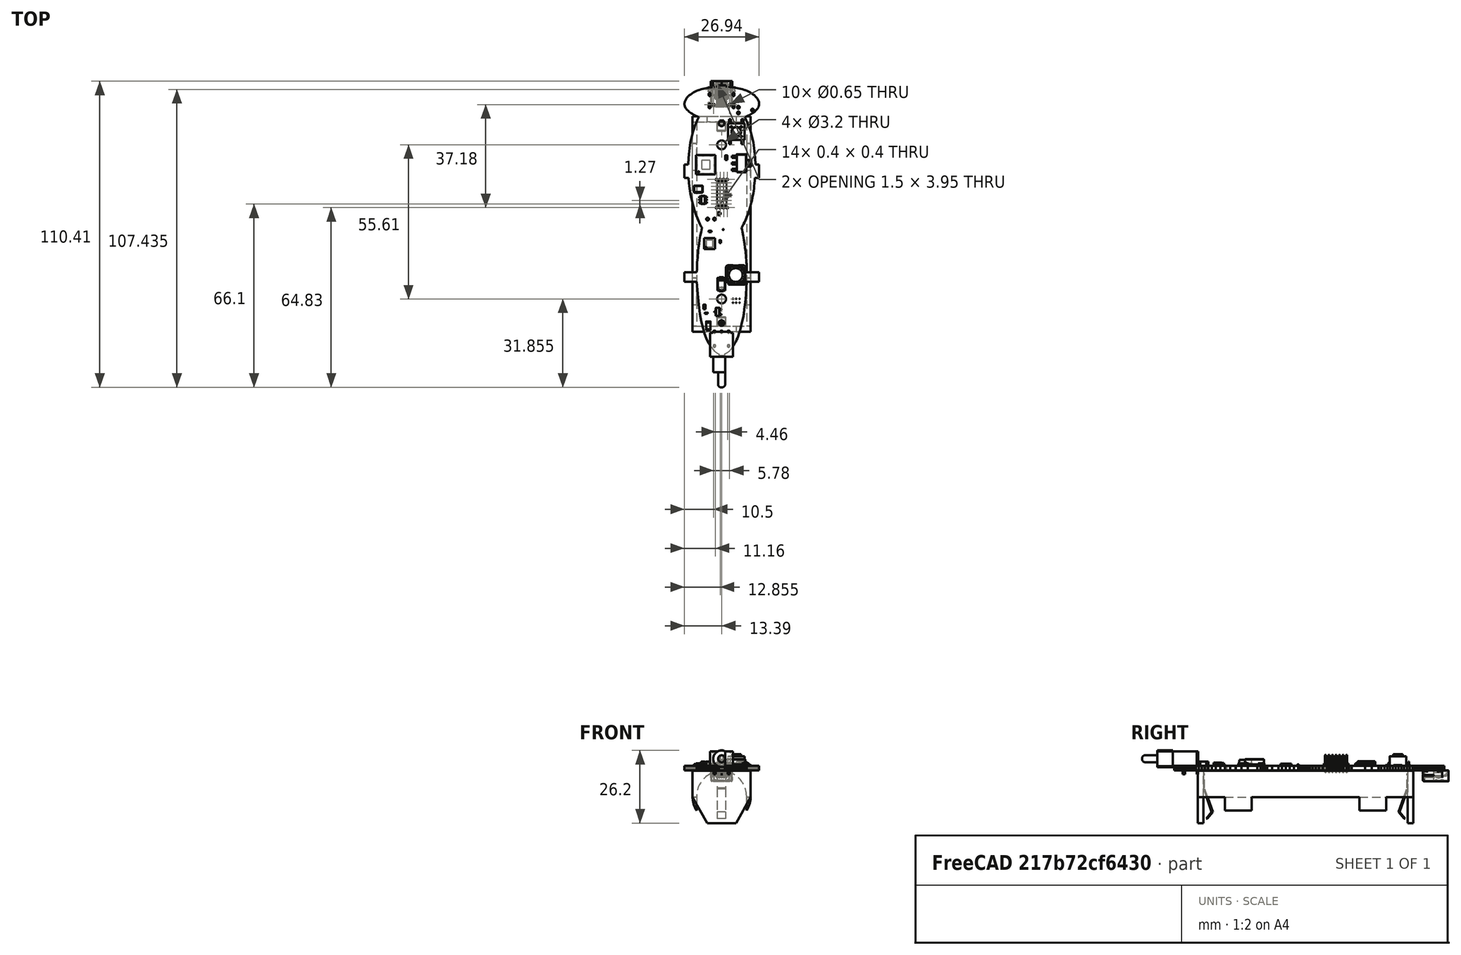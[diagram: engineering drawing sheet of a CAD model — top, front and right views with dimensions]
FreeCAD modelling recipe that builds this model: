
FCSTD DOCUMENT  (FreeCAD 0.21R30454 (Git))
Label: centerBoard
License: All rights reserved
LicenseURL: http://en.wikipedia.org/wiki/All_rights_reserved
objects: App::Link×64, Part::Feature×20, App::Part×5, PartDesign::CoordinateSystem×1, Sketcher::SketchObject×1
note: 22 computed .brp shape members not serialized (recipe doc carries the construction recipe); baked Part::Feature solids carry a one-line shape summary decoded from their .brp

FEATURE [PartDesign::CoordinateSystem] Local_CS_931
  AttacherType = Attacher::AttachEngine3D
  MapMode = 2
  Support = -> [X_Axis001]
FEATURE [Part::Feature] Pcb_931
  shape: bbox 26.94 x 97.45 x 1.6 mm, 316 faces (baked)
FEATURE [Sketcher::SketchObject] PCB_Sketch_931
  FullyConstrained = false
  sketch-geometry (258):
    g0: LineSegment StartX=204.611 StartY=-59.7706 StartZ=0 EndX=204.161 EndY=-58.747 EndZ=0
    g1: LineSegment StartX=207.307 StartY=-79.6422 StartZ=0 EndX=208.849 EndY=-79.6422 EndZ=0
    g2: LineSegment StartX=203.133 StartY=-100.504 StartZ=0 EndX=202.842 EndY=-99.0355 EndZ=0
    g3: LineSegment StartX=198.204 StartY=-141.964 StartZ=0 EndX=198.335 EndY=-141.829 EndZ=0
    g4: LineSegment StartX=196.821 StartY=-46.2543 StartZ=0 EndX=195.381 EndY=-46.2543 EndZ=0
    g5: LineSegment StartX=186.994 StartY=-104.828 StartZ=0 EndX=186.849 EndY=-106.147 EndZ=0
    g6: LineSegment StartX=190.699 StartY=-139.374 StartZ=0 EndX=191.002 EndY=-139.905 EndZ=0
    g7: LineSegment StartX=194.282 StartY=-143.161 StartZ=0 EndX=194.282 EndY=-143.702 EndZ=0
    g8: LineSegment StartX=206.155 StartY=-49.1673 StartZ=0 EndX=205.642 EndY=-48.8567 EndZ=0
    g9: LineSegment StartX=207.546 StartY=-55.4632 StartZ=0 EndX=207.833 EndY=-55.1801 EndZ=0
    g10: LineSegment StartX=191.879 StartY=-141.193 StartZ=0 EndX=192.157 EndY=-141.532 EndZ=0
    g11: LineSegment StartX=186.361 StartY=-117.075 StartZ=0 EndX=186.651 EndY=-121.509 EndZ=0
    g12: LineSegment StartX=208.789 StartY=-53.5041 StartZ=0 EndX=208.834 EndY=-53.2317 EndZ=0
    g13: LineSegment StartX=206.019 StartY=-88.581 StartZ=0 EndX=206.204 EndY=-87.8001 EndZ=0
    g14: LineSegment StartX=203.931 StartY=-123.5 StartZ=0 EndX=204.11 EndY=-121.509 EndZ=0
    g15: LineSegment StartX=183.585 StartY=-81.6183 StartZ=0 EndX=183.791 EndY=-83.5056 EndZ=0
    g16: LineSegment StartX=201.902 StartY=-134.849 StartZ=0 EndX=202.197 EndY=-133.815 EndZ=0
    g17: LineSegment StartX=202.746 StartY=-97.2753 StartZ=0 EndX=202.978 EndY=-96.8717 EndZ=0
    g18: LineSegment StartX=202.76 StartY=-131.45 StartZ=0 EndX=203.025 EndY=-130.106 EndZ=0
    g19: LineSegment StartX=184.261 StartY=-65.7953 StartZ=0 EndX=184.058 EndY=-66.826 EndZ=0
    g20: LineSegment StartX=202.505 StartY=-97.6016 StartZ=0 EndX=202.585 EndY=-97.5204 EndZ=0
    g21: LineSegment StartX=196.48 StartY=-143.161 StartZ=0 EndX=196.623 EndY=-143.098 EndZ=0
    g22: LineSegment StartX=185.289 StartY=-56.8742 StartZ=0 EndX=185.841 EndY=-57.153 EndZ=0
    g23: LineSegment StartX=208.834 StartY=-53.2317 StartZ=0 EndX=208.851 EndY=-52.9624 EndZ=0
    g24: LineSegment StartX=204.4 StartY=-117.075 StartZ=0 EndX=208.849 EndY=-117.075 EndZ=0
    g25: LineSegment StartX=185.651 StartY=-48.576 StartZ=0 EndX=185.119 EndY=-48.8567 EndZ=0
    g26: LineSegment StartX=200.369 StartY=-138.788 StartZ=0 EndX=200.678 EndY=-138.143 EndZ=0
    g27: LineSegment StartX=185.964 StartY=-92.6642 StartZ=0 EndX=186.78 EndY=-94.7637 EndZ=0
    g28: LineSegment StartX=198.468 StartY=-141.686 StartZ=0 EndX=198.604 EndY=-141.532 EndZ=0
    g29: LineSegment StartX=200.262 StartY=-47.1518 StartZ=0 EndX=199.594 EndY=-47.0453 EndZ=0
    g30: LineSegment StartX=186.393 StartY=-112.527 StartZ=0 EndX=186.377 EndY=-113.724 EndZ=0
    g31: LineSegment StartX=182.209 StartY=-51.6716 StartZ=0 EndX=182.103 EndY=-51.9211 EndZ=0
    g32: LineSegment StartX=187.169 StartY=-103.429 StartZ=0 EndX=186.994 EndY=-104.828 EndZ=0
    g33: LineSegment StartX=197.156 StartY=-142.81 StartZ=0 EndX=197.366 EndY=-142.672 EndZ=0
    g34: LineSegment StartX=203.992 StartY=-48.0954 StartZ=0 EndX=203.408 EndY=-47.8915 EndZ=0
    g35: LineSegment StartX=200.678 StartY=-138.143 StartZ=0 EndX=200.987 EndY=-137.433 EndZ=0
    g36: LineSegment StartX=191.301 StartY=-140.383 StartZ=0 EndX=191.593 EndY=-140.811 EndZ=0
    g37: LineSegment StartX=186.503 StartY=-110.129 StartZ=0 EndX=186.46 EndY=-110.807 EndZ=0
    g38: LineSegment StartX=183.377 StartY=-72.3896 StartZ=0 EndX=183.215 EndY=-74.8986 EndZ=0
    g39: LineSegment StartX=206.647 StartY=-49.5098 StartZ=0 EndX=206.155 EndY=-49.1673 EndZ=0
    g40: LineSegment StartX=201.601 StartY=-135.792 StartZ=0 EndX=201.902 EndY=-134.849 EndZ=0
    g41: LineSegment StartX=203.408 StartY=-47.8915 StartZ=0 EndX=202.807 EndY=-47.709 EndZ=0
    g42: LineSegment StartX=208.428 StartY=-51.4271 StartZ=0 EndX=208.284 EndY=-51.188 EndZ=0
    g43: LineSegment StartX=182.294 StartY=-54.3351 StartZ=0 EndX=182.469 EndY=-54.6157 EndZ=0
    g44: LineSegment StartX=185.119 StartY=-48.8567 StartZ=0 EndX=184.607 EndY=-49.1673 EndZ=0
    g45: LineSegment StartX=204.382 StartY=-93.7798 StartZ=0 EndX=204.798 EndY=-92.6642 EndZ=0
    g46: LineSegment StartX=183.215 StartY=-74.8986 StartZ=0 EndX=181.912 EndY=-74.8986 EndZ=0
    g47: LineSegment StartX=205.216 StartY=-91.4223 StartZ=0 EndX=205.627 EndY=-90.0595 EndZ=0
    g48: LineSegment StartX=208.849 StartY=-74.8986 StartZ=0 EndX=207.546 EndY=-74.8986 EndZ=0
    g49: LineSegment StartX=186.651 StartY=-121.509 StartZ=0 EndX=187.031 EndY=-125.349 EndZ=0
    g50: LineSegment StartX=204.125 StartY=-108.431 StartZ=0 EndX=203.913 EndY=-106.147 EndZ=0
    g51: LineSegment StartX=187.38 StartY=-101.978 StartZ=0 EndX=187.169 EndY=-103.429 EndZ=0
    g52: LineSegment StartX=183.913 StartY=-56.0295 StartZ=0 EndX=184.326 EndY=-56.3121 EndZ=0
    g53: LineSegment StartX=205.11 StartY=-48.576 StartZ=0 EndX=204.56 EndY=-48.3229 EndZ=0
    g54: LineSegment StartX=201.561 StartY=-47.4 StartZ=0 EndX=200.918 EndY=-47.2693 EndZ=0
    g55: LineSegment StartX=204.258 StartY=-110.129 StartZ=0 EndX=204.2 EndY=-109.347 EndZ=0
    g56: LineSegment StartX=193.978 StartY=-143.02 StartZ=0 EndX=194.282 EndY=-143.161 EndZ=0
    g57: LineSegment StartX=181.958 StartY=-52.4338 StartZ=0 EndX=181.922 EndY=-52.6963 EndZ=0
    g58: LineSegment StartX=204.798 StartY=-92.6642 StartZ=0 EndX=205.216 EndY=-91.4223 EndZ=0
    g59: LineSegment StartX=204.302 StartY=-110.807 StartZ=0 EndX=204.258 EndY=-110.129 EndZ=0
    g60: LineSegment StartX=196.623 StartY=-143.098 StartZ=0 EndX=196.784 EndY=-143.02 EndZ=0
    g61: LineSegment StartX=198.227 StartY=-46.857 StartZ=0 EndX=196.821 EndY=-46.6878 EndZ=0
    g62: LineSegment StartX=204.56 StartY=-48.3229 StartZ=0 EndX=203.992 EndY=-48.0954 EndZ=0
    g63: LineSegment StartX=183.726 StartY=-68.9546 StartZ=0 EndX=183.593 EndY=-70.0623 EndZ=0
    g64: LineSegment StartX=200.215 StartY=-139.088 StartZ=0 EndX=200.369 EndY=-138.788 EndZ=0
    g65: LineSegment StartX=207.117 StartY=-49.8853 StartZ=0 EndX=206.647 EndY=-49.5098 EndZ=0
    g66: LineSegment StartX=181.972 StartY=-53.5041 StartZ=0 EndX=182.047 EndY=-53.779 EndZ=0
    g67: LineSegment StartX=184.607 StartY=-49.1673 StartZ=0 EndX=184.114 EndY=-49.5098 EndZ=0
    g68: LineSegment StartX=199.61 StartY=-140.15 StartZ=0 EndX=199.759 EndY=-139.905 EndZ=0
    g69: LineSegment StartX=205.627 StartY=-90.0595 StartZ=0 EndX=206.019 EndY=-88.581 EndZ=0
    g70: LineSegment StartX=202.679 StartY=-98.3125 StartZ=0 EndX=202.505 EndY=-97.6016 EndZ=0
    g71: LineSegment StartX=196.962 StartY=-142.925 StartZ=0 EndX=197.156 EndY=-142.81 EndZ=0
    g72: LineSegment StartX=206.204 StartY=-87.8001 StartZ=0 EndX=206.381 EndY=-86.9923 EndZ=0
    g73: LineSegment StartX=198.604 StartY=-141.532 StartZ=0 EndX=198.742 EndY=-141.368 EndZ=0
    g74: LineSegment StartX=189.774 StartY=-137.433 StartZ=0 EndX=190.393 EndY=-138.788 EndZ=0
    g75: LineSegment StartX=184.058 StartY=-66.826 StartZ=0 EndX=183.88 EndY=-67.8774 EndZ=0
    g76: LineSegment StartX=189.16 StartY=-135.792 StartZ=0 EndX=189.774 EndY=-137.433 EndZ=0
    g77: LineSegment StartX=186.151 StartY=-59.7706 StartZ=0 EndX=185.743 EndY=-60.7805 EndZ=0
    g78: LineSegment StartX=206.381 StartY=-86.9923 StartZ=0 EndX=206.547 EndY=-86.1583 EndZ=0
    g79: LineSegment StartX=208.84 StartY=-52.6963 StartZ=0 EndX=208.803 EndY=-52.4338 EndZ=0
    g80: LineSegment StartX=204.318 StartY=-57.4299 StartZ=0 EndX=204.92 EndY=-57.153 EndZ=0
    g81: LineSegment StartX=188.015 StartY=-97.2753 StartZ=0 EndX=188.257 EndY=-97.6016 EndZ=0
    g82: LineSegment StartX=205.472 StartY=-56.8742 StartZ=0 EndX=205.977 EndY=-56.5938 EndZ=0
    g83: LineSegment StartX=185.134 StartY=-90.0595 StartZ=0 EndX=185.545 EndY=-91.4223 EndZ=0
    g84: LineSegment StartX=203.512 StartY=-127.062 StartZ=0 EndX=203.731 EndY=-125.349 EndZ=0
    g85: LineSegment StartX=202.807 StartY=-47.709 StartZ=0 EndX=202.191 EndY=-47.5458 EndZ=0
    g86: LineSegment StartX=189.843 StartY=-47.2693 StartZ=0 EndX=189.2 EndY=-47.4 EndZ=0
    g87: LineSegment StartX=203.025 StartY=-130.106 StartZ=0 EndX=203.276 EndY=-128.645 EndZ=0
    g88: LineSegment StartX=199.314 StartY=-140.603 StartZ=0 EndX=199.461 EndY=-140.383 EndZ=0
    g89: LineSegment StartX=207.169 StartY=-70.0623 StartZ=0 EndX=207.035 EndY=-68.9546 EndZ=0
    g90: LineSegment StartX=199.461 StartY=-140.383 StartZ=0 EndX=199.61 EndY=-140.15 EndZ=0
    g91: LineSegment StartX=191.002 StartY=-139.905 StartZ=0 EndX=191.301 EndY=-140.383 EndZ=0
    g92: LineSegment StartX=186.46 StartY=-110.807 StartZ=0 EndX=186.429 EndY=-111.412 EndZ=0
    g93: LineSegment StartX=182.638 StartY=-50.9546 StartZ=0 EndX=182.477 EndY=-51.188 EndZ=0
    g94: LineSegment StartX=196.821 StartY=-46.6878 StartZ=0 EndX=196.821 EndY=-46.2543 EndZ=0
    g95: LineSegment StartX=183.543 StartY=-55.7465 StartZ=0 EndX=183.913 EndY=-56.0295 EndZ=0
    g96: LineSegment StartX=181.912 StartY=-117.075 StartZ=0 EndX=186.361 EndY=-117.075 EndZ=0
    g97: LineSegment StartX=204.2 StartY=-109.347 StartZ=0 EndX=204.125 EndY=-108.431 EndZ=0
    g98: LineSegment StartX=181.911 StartY=-52.9624 StartZ=0 EndX=181.927 EndY=-53.2317 EndZ=0
    g99: LineSegment StartX=206.702 StartY=-85.2987 StartZ=0 EndX=206.844 EndY=-84.4142 EndZ=0
    g100: LineSegment StartX=208.742 StartY=-52.1753 StartZ=0 EndX=208.658 EndY=-51.9211 EndZ=0
    g101: LineSegment StartX=192.686 StartY=-142.089 StartZ=0 EndX=192.935 EndY=-142.314 EndZ=0
    g102: LineSegment StartX=187.095 StartY=-57.7046 StartZ=0 EndX=186.6 EndY=-58.747 EndZ=0
    g103: LineSegment StartX=208.849 StartY=-117.075 StartZ=0 EndX=208.849 EndY=-113.724 EndZ=0
    g104: LineSegment StartX=196.784 StartY=-143.02 StartZ=0 EndX=196.962 EndY=-142.925 EndZ=0
    g105: LineSegment StartX=186.6 StartY=-58.747 StartZ=0 EndX=186.151 EndY=-59.7706 EndZ=0
    g106: LineSegment StartX=184.785 StartY=-56.5938 StartZ=0 EndX=185.289 EndY=-56.8742 EndZ=0
    g107: LineSegment StartX=198.882 StartY=-141.193 StartZ=0 EndX=199.024 EndY=-141.008 EndZ=0
    g108: LineSegment StartX=191.167 StartY=-47.0453 StartZ=0 EndX=189.843 EndY=-47.2693 EndZ=0
    g109: LineSegment StartX=182.103 StartY=-51.9211 StartZ=0 EndX=182.019 EndY=-52.1753 EndZ=0
    g110: LineSegment StartX=200.918 StartY=-47.2693 StartZ=0 EndX=200.262 EndY=-47.1518 EndZ=0
    g111: LineSegment StartX=203.268 StartY=-96.315 StartZ=0 EndX=203.607 EndY=-95.6105 EndZ=0
    g112: LineSegment StartX=188.565 StartY=-133.815 StartZ=0 EndX=189.16 EndY=-135.792 EndZ=0
    g113: LineSegment StartX=207.218 StartY=-55.7465 StartZ=0 EndX=207.546 EndY=-55.4632 EndZ=0
    g114: LineSegment StartX=207.252 StartY=-80.641 StartZ=0 EndX=207.307 EndY=-79.6422 EndZ=0
    g115: LineSegment StartX=188.257 StartY=-97.6016 StartZ=0 EndX=187.92 EndY=-99.0355 EndZ=0
    g116: LineSegment StartX=186.443 StartY=-57.4299 StartZ=0 EndX=187.095 EndY=-57.7046 EndZ=0
    g117: LineSegment StartX=203.607 StartY=-95.6105 StartZ=0 EndX=203.982 EndY=-94.7637 EndZ=0
    g118: LineSegment StartX=207.554 StartY=-50.2921 StartZ=0 EndX=207.117 EndY=-49.8853 EndZ=0
    g119: LineSegment StartX=185.841 StartY=-57.153 StartZ=0 EndX=186.443 EndY=-57.4299 EndZ=0
    g120: LineSegment StartX=204.267 StartY=-119.37 StartZ=0 EndX=204.4 EndY=-117.075 EndZ=0
    g121: LineSegment StartX=199.168 StartY=-140.811 StartZ=0 EndX=199.314 EndY=-140.603 EndZ=0
    g122: LineSegment StartX=199.91 StartY=-139.646 StartZ=0 EndX=200.062 EndY=-139.374 EndZ=0
    g123: LineSegment StartX=203.731 StartY=-125.349 StartZ=0 EndX=203.931 EndY=-123.5 EndZ=0
    g124: LineSegment StartX=206.844 StartY=-84.4142 StartZ=0 EndX=206.971 EndY=-83.5056 EndZ=0
    g125: LineSegment StartX=203.913 StartY=-106.147 StartZ=0 EndX=203.768 EndY=-104.828 EndZ=0
    g126: LineSegment StartX=206.848 StartY=-56.0295 StartZ=0 EndX=207.218 EndY=-55.7465 EndZ=0
    g127: LineSegment StartX=198.335 StartY=-141.829 StartZ=0 EndX=198.468 EndY=-141.686 EndZ=0
    g128: LineSegment StartX=204.333 StartY=-111.412 StartZ=0 EndX=204.302 EndY=-110.807 EndZ=0
    g129: LineSegment StartX=183.004 StartY=-50.5063 StartZ=0 EndX=182.814 EndY=-50.7272 EndZ=0
    g130: LineSegment StartX=183.88 StartY=-67.8774 StartZ=0 EndX=183.726 EndY=-68.9546 EndZ=0
    g131: LineSegment StartX=181.912 StartY=-79.6422 StartZ=0 EndX=183.454 EndY=-79.6422 EndZ=0
    g132: LineSegment StartX=198.075 StartY=-142.089 StartZ=0 EndX=198.204 EndY=-141.964 EndZ=0
    g133: LineSegment StartX=200.062 StartY=-139.374 StartZ=0 EndX=200.215 EndY=-139.088 EndZ=0
    g134: LineSegment StartX=185.545 StartY=-91.4223 StartZ=0 EndX=185.964 EndY=-92.6642 EndZ=0
    g135: LineSegment StartX=202.978 StartY=-96.8717 StartZ=0 EndX=203.268 EndY=-96.315 EndZ=0
    g136: LineSegment StartX=205.018 StartY=-60.7805 StartZ=0 EndX=204.611 EndY=-59.7706 EndZ=0
    g137: LineSegment StartX=187.954 StartY=-47.709 StartZ=0 EndX=187.354 EndY=-47.8915 EndZ=0
    g138: LineSegment StartX=208.292 StartY=-54.6157 StartZ=0 EndX=208.467 EndY=-54.3351 EndZ=0
    g139: LineSegment StartX=187.92 StartY=-99.0355 StartZ=0 EndX=187.629 EndY=-100.504 EndZ=0
    g140: LineSegment StartX=208.658 StartY=-51.9211 StartZ=0 EndX=208.553 EndY=-51.6716 EndZ=0
    g141: LineSegment StartX=188.002 StartY=-131.45 StartZ=0 EndX=188.565 EndY=-133.815 EndZ=0
    g142: LineSegment StartX=204.11 StartY=-121.509 StartZ=0 EndX=204.267 EndY=-119.37 EndZ=0
    g143: LineSegment StartX=196.48 StartY=-143.702 StartZ=0 EndX=196.48 EndY=-143.161 EndZ=0
    g144: LineSegment StartX=183.791 StartY=-83.5056 StartZ=0 EndX=184.059 EndY=-85.2987 EndZ=0
    g145: LineSegment StartX=193.605 StartY=-142.81 StartZ=0 EndX=193.8 EndY=-142.925 EndZ=0
    g146: LineSegment StartX=186.636 StartY=-108.431 StartZ=0 EndX=186.503 EndY=-110.129 EndZ=0
    g147: LineSegment StartX=192.535 StartY=-46.857 StartZ=0 EndX=191.167 EndY=-47.0453 EndZ=0
    g148: LineSegment StartX=198.742 StartY=-141.368 StartZ=0 EndX=198.882 EndY=-141.193 EndZ=0
    g149: LineSegment StartX=182.814 StartY=-50.7272 StartZ=0 EndX=182.638 EndY=-50.9546 EndZ=0
    g150: LineSegment StartX=187.031 StartY=-125.349 StartZ=0 EndX=187.486 EndY=-128.645 EndZ=0
    g151: LineSegment StartX=183.421 StartY=-50.085 StartZ=0 EndX=183.207 EndY=-50.2921 EndZ=0
    g152: LineSegment StartX=204.368 StartY=-112.527 StartZ=0 EndX=204.354 EndY=-111.975 EndZ=0
    g153: LineSegment StartX=202.585 StartY=-97.5204 StartZ=0 EndX=202.746 EndY=-97.2753 EndZ=0
    g154: LineSegment StartX=184.742 StartY=-88.581 StartZ=0 EndX=185.134 EndY=-90.0595 EndZ=0
    g155: LineSegment StartX=183.454 StartY=-79.6422 StartZ=0 EndX=183.585 EndY=-81.6183 EndZ=0
    g156: LineSegment StartX=206.971 StartY=-83.5056 StartZ=0 EndX=207.082 EndY=-82.5734 EndZ=0
    g157: LineSegment StartX=206.704 StartY=-66.826 StartZ=0 EndX=206.501 EndY=-65.7953 EndZ=0
    g158: LineSegment StartX=203.592 StartY=-103.429 StartZ=0 EndX=203.382 EndY=-101.978 EndZ=0
    g159: LineSegment StartX=208.714 StartY=-53.779 StartZ=0 EndX=208.789 EndY=-53.5041 EndZ=0
    g160: LineSegment StartX=203.276 StartY=-128.645 StartZ=0 EndX=203.512 EndY=-127.062 EndZ=0
    g161: LineSegment StartX=186.429 StartY=-111.412 StartZ=0 EndX=186.393 EndY=-112.527 EndZ=0
    g162: LineSegment StartX=197.826 StartY=-142.314 StartZ=0 EndX=198.075 EndY=-142.089 EndZ=0
    g163: LineSegment StartX=193.396 StartY=-142.672 StartZ=0 EndX=193.605 EndY=-142.81 EndZ=0
    g164: LineSegment StartX=208.851 StartY=-52.9624 StartZ=0 EndX=208.84 EndY=-52.6963 EndZ=0
    g165: LineSegment StartX=197.59 StartY=-142.507 StartZ=0 EndX=197.826 EndY=-142.314 EndZ=0
    g166: LineSegment StartX=206.009 StartY=-63.7765 StartZ=0 EndX=205.715 EndY=-62.7784 EndZ=0
    g167: LineSegment StartX=185.743 StartY=-60.7805 StartZ=0 EndX=185.376 EndY=-61.7814 EndZ=0
    g168: LineSegment StartX=195.381 StartY=-143.702 StartZ=0 EndX=196.48 EndY=-143.702 EndZ=0
    g169: LineSegment StartX=183.593 StartY=-70.0623 StartZ=0 EndX=183.377 EndY=-72.3896 EndZ=0
    g170: LineSegment StartX=206.501 StartY=-65.7953 StartZ=0 EndX=206.27 EndY=-64.7804 EndZ=0
    g171: LineSegment StartX=200.987 StartY=-137.433 StartZ=0 EndX=201.296 EndY=-136.651 EndZ=0
    g172: LineSegment StartX=191.593 StartY=-140.811 StartZ=0 EndX=191.879 EndY=-141.193 EndZ=0
    g173: LineSegment StartX=182.154 StartY=-54.0561 StartZ=0 EndX=182.294 EndY=-54.3351 EndZ=0
    g174: LineSegment StartX=208.607 StartY=-54.0561 StartZ=0 EndX=208.714 EndY=-53.779 EndZ=0
    g175: LineSegment StartX=182.047 StartY=-53.779 StartZ=0 EndX=182.154 EndY=-54.0561 EndZ=0
    g176: LineSegment StartX=199.024 StartY=-141.008 StartZ=0 EndX=199.168 EndY=-140.811 EndZ=0
    g177: LineSegment StartX=192.935 StartY=-142.314 StartZ=0 EndX=193.172 EndY=-142.507 EndZ=0
    g178: LineSegment StartX=189.2 StartY=-47.4 StartZ=0 EndX=188.57 EndY=-47.5458 EndZ=0
    g179: LineSegment StartX=182.68 StartY=-54.8975 StartZ=0 EndX=182.928 EndY=-55.1801 EndZ=0
    g180: LineSegment StartX=186.377 StartY=-113.724 StartZ=0 EndX=181.912 EndY=-113.724 EndZ=0
    g181: LineSegment StartX=202.483 StartY=-132.685 StartZ=0 EndX=202.76 EndY=-131.45 EndZ=0
    g182: LineSegment StartX=183.216 StartY=-55.4632 StartZ=0 EndX=183.543 EndY=-55.7465 EndZ=0
    g183: LineSegment StartX=206.435 StartY=-56.3121 StartZ=0 EndX=206.848 EndY=-56.0295 EndZ=0
    g184: LineSegment StartX=184.326 StartY=-56.3121 StartZ=0 EndX=184.785 EndY=-56.5938 EndZ=0
    g185: LineSegment StartX=184.753 StartY=-63.7765 StartZ=0 EndX=184.492 EndY=-64.7804 EndZ=0
    g186: LineSegment StartX=206.27 StartY=-64.7804 StartZ=0 EndX=206.009 EndY=-63.7765 EndZ=0
    g187: LineSegment StartX=186.202 StartY=-48.3229 StartZ=0 EndX=185.651 EndY=-48.576 EndZ=0
    g188: LineSegment StartX=205.385 StartY=-61.7814 StartZ=0 EndX=205.018 EndY=-60.7805 EndZ=0
    g189: LineSegment StartX=208.467 StartY=-54.3351 StartZ=0 EndX=208.607 EndY=-54.0561 EndZ=0
    g190: LineSegment StartX=187.629 StartY=-100.504 StartZ=0 EndX=187.38 EndY=-101.978 EndZ=0
    g191: LineSegment StartX=207.176 StartY=-81.6183 StartZ=0 EndX=207.252 EndY=-80.641 EndZ=0
    g192: LineSegment StartX=208.082 StartY=-54.8975 StartZ=0 EndX=208.292 EndY=-54.6157 EndZ=0
    g193: LineSegment StartX=204.385 StartY=-113.724 StartZ=0 EndX=204.368 EndY=-112.527 EndZ=0
    g194: LineSegment StartX=208.849 StartY=-113.724 StartZ=0 EndX=204.385 EndY=-113.724 EndZ=0
    g195: LineSegment StartX=201.296 StartY=-136.651 StartZ=0 EndX=201.601 EndY=-135.792 EndZ=0
    g196: LineSegment StartX=183.207 StartY=-50.2921 StartZ=0 EndX=183.004 EndY=-50.5063 EndZ=0
    g197: LineSegment StartX=188.57 StartY=-47.5458 StartZ=0 EndX=187.954 EndY=-47.709 EndZ=0
    g198: LineSegment StartX=190.393 StartY=-138.788 StartZ=0 EndX=190.699 EndY=-139.374 EndZ=0
    g199: LineSegment StartX=185.047 StartY=-62.7784 StartZ=0 EndX=184.753 EndY=-63.7765 EndZ=0
    g200: LineSegment StartX=199.594 StartY=-47.0453 StartZ=0 EndX=198.227 EndY=-46.857 EndZ=0
    g201: LineSegment StartX=204.92 StartY=-57.153 StartZ=0 EndX=205.472 EndY=-56.8742 EndZ=0
    g202: LineSegment StartX=207.546 StartY=-74.8986 StartZ=0 EndX=207.384 EndY=-72.3896 EndZ=0
    g203: LineSegment StartX=208.849 StartY=-79.6422 StartZ=0 EndX=208.849 EndY=-74.8986 EndZ=0
    g204: LineSegment StartX=203.382 StartY=-101.978 StartZ=0 EndX=203.133 EndY=-100.504 EndZ=0
    g205: LineSegment StartX=205.977 StartY=-56.5938 StartZ=0 EndX=206.435 EndY=-56.3121 EndZ=0
    g206: LineSegment StartX=185.376 StartY=-61.7814 StartZ=0 EndX=185.047 EndY=-62.7784 EndZ=0
    g207: LineSegment StartX=184.38 StartY=-86.9923 StartZ=0 EndX=184.742 EndY=-88.581 EndZ=0
    g208: LineSegment StartX=193.8 StartY=-142.925 StartZ=0 EndX=193.978 EndY=-143.02 EndZ=0
    g209: LineSegment StartX=181.912 StartY=-74.8986 StartZ=0 EndX=181.912 EndY=-79.6422 EndZ=0
    g210: LineSegment StartX=182.334 StartY=-51.4271 StartZ=0 EndX=182.209 EndY=-51.6716 EndZ=0
    g211: LineSegment StartX=195.381 StartY=-46.2543 StartZ=0 EndX=193.94 EndY=-46.2543 EndZ=0
    g212: LineSegment StartX=181.922 StartY=-52.6963 StartZ=0 EndX=181.911 EndY=-52.9624 EndZ=0
    g213: LineSegment StartX=192.427 StartY=-141.829 StartZ=0 EndX=192.686 EndY=-142.089 EndZ=0
    g214: LineSegment StartX=208.284 StartY=-51.188 StartZ=0 EndX=208.123 EndY=-50.9546 EndZ=0
    g215: LineSegment StartX=186.769 StartY=-48.0954 StartZ=0 EndX=186.202 EndY=-48.3229 EndZ=0
    g216: LineSegment StartX=202.191 StartY=-47.5458 StartZ=0 EndX=201.561 EndY=-47.4 EndZ=0
    g217: LineSegment StartX=183.644 StartY=-49.8853 StartZ=0 EndX=183.421 EndY=-50.085 EndZ=0
    g218: LineSegment StartX=187.354 StartY=-47.8915 StartZ=0 EndX=186.769 EndY=-48.0954 EndZ=0
    g219: LineSegment StartX=197.366 StartY=-142.672 StartZ=0 EndX=197.59 EndY=-142.507 EndZ=0
    g220: LineSegment StartX=207.947 StartY=-50.7272 StartZ=0 EndX=207.554 EndY=-50.2921 EndZ=0
    g221: LineSegment StartX=187.493 StartY=-96.315 StartZ=0 EndX=188.015 EndY=-97.2753 EndZ=0
    g222: LineSegment StartX=192.157 StartY=-141.532 StartZ=0 EndX=192.427 EndY=-141.829 EndZ=0
    g223: LineSegment StartX=184.059 StartY=-85.2987 StartZ=0 EndX=184.38 EndY=-86.9923 EndZ=0
    g224: LineSegment StartX=181.927 StartY=-53.2317 StartZ=0 EndX=181.972 EndY=-53.5041 EndZ=0
    g225: LineSegment StartX=202.197 StartY=-133.815 StartZ=0 EndX=202.483 EndY=-132.685 EndZ=0
    g226: LineSegment StartX=194.282 StartY=-143.702 StartZ=0 EndX=195.381 EndY=-143.702 EndZ=0
    g227: LineSegment StartX=203.982 StartY=-94.7637 StartZ=0 EndX=204.382 EndY=-93.7798 EndZ=0
    g228: LineSegment StartX=184.492 StartY=-64.7804 StartZ=0 EndX=184.261 EndY=-65.7953 EndZ=0
    g229: LineSegment StartX=193.172 StartY=-142.507 StartZ=0 EndX=193.396 EndY=-142.672 EndZ=0
    g230: LineSegment StartX=182.928 StartY=-55.1801 StartZ=0 EndX=183.216 EndY=-55.4632 EndZ=0
    g231: LineSegment StartX=204.161 StartY=-58.747 StartZ=0 EndX=203.666 EndY=-57.7046 EndZ=0
    g232: LineSegment StartX=182.477 StartY=-51.188 StartZ=0 EndX=182.334 EndY=-51.4271 EndZ=0
    g233: LineSegment StartX=199.759 StartY=-139.905 StartZ=0 EndX=199.91 EndY=-139.646 EndZ=0
    g234: LineSegment StartX=187.486 StartY=-128.645 StartZ=0 EndX=188.002 EndY=-131.45 EndZ=0
    g235: LineSegment StartX=205.642 StartY=-48.8567 StartZ=0 EndX=205.11 EndY=-48.576 EndZ=0
    g236: LineSegment StartX=207.035 StartY=-68.9546 StartZ=0 EndX=206.881 EndY=-67.8774 EndZ=0
    g237: LineSegment StartX=181.912 StartY=-113.724 StartZ=0 EndX=181.912 EndY=-117.075 EndZ=0
    g238: LineSegment StartX=208.553 StartY=-51.6716 StartZ=0 EndX=208.428 EndY=-51.4271 EndZ=0
    g239: LineSegment StartX=202.842 StartY=-99.0355 StartZ=0 EndX=202.679 EndY=-98.3125 EndZ=0
    g240: LineSegment StartX=207.384 StartY=-72.3896 StartZ=0 EndX=207.169 EndY=-70.0623 EndZ=0
    g241: LineSegment StartX=186.849 StartY=-106.147 StartZ=0 EndX=186.636 EndY=-108.431 EndZ=0
    g242: LineSegment StartX=208.803 StartY=-52.4338 StartZ=0 EndX=208.742 EndY=-52.1753 EndZ=0
    g243: LineSegment StartX=182.469 StartY=-54.6157 StartZ=0 EndX=182.68 EndY=-54.8975 EndZ=0
    g244: LineSegment StartX=182.019 StartY=-52.1753 StartZ=0 EndX=181.958 EndY=-52.4338 EndZ=0
    g245: LineSegment StartX=203.768 StartY=-104.828 StartZ=0 EndX=203.592 EndY=-103.429 EndZ=0
    g246: LineSegment StartX=206.547 StartY=-86.1583 StartZ=0 EndX=206.702 EndY=-85.2987 EndZ=0
    g247: LineSegment StartX=207.082 StartY=-82.5734 StartZ=0 EndX=207.176 EndY=-81.6183 EndZ=0
    g248: LineSegment StartX=184.114 StartY=-49.5098 StartZ=0 EndX=183.644 EndY=-49.8853 EndZ=0
    g249: LineSegment StartX=207.833 StartY=-55.1801 StartZ=0 EndX=208.082 EndY=-54.8975 EndZ=0
    g250: LineSegment StartX=193.94 StartY=-46.2543 StartZ=0 EndX=193.94 EndY=-46.6878 EndZ=0
    g251: LineSegment StartX=206.881 StartY=-67.8774 StartZ=0 EndX=206.704 EndY=-66.826 EndZ=0
    g252: LineSegment StartX=186.78 StartY=-94.7637 StartZ=0 EndX=187.493 EndY=-96.315 EndZ=0
    g253: LineSegment StartX=204.354 StartY=-111.975 StartZ=0 EndX=204.333 EndY=-111.412 EndZ=0
    g254: LineSegment StartX=203.666 StartY=-57.7046 StartZ=0 EndX=204.318 EndY=-57.4299 EndZ=0
    g255: LineSegment StartX=208.123 StartY=-50.9546 StartZ=0 EndX=207.947 EndY=-50.7272 EndZ=0
    g256: LineSegment StartX=205.715 StartY=-62.7784 StartZ=0 EndX=205.385 EndY=-61.7814 EndZ=0
    g257: LineSegment StartX=193.94 StartY=-46.6878 StartZ=0 EndX=192.535 EndY=-46.857 EndZ=0
  constraints (258):
    c: Coincident(g96,g237)
    c: Coincident(g180,g237)
    c: Coincident(g131,g209)
    c: Coincident(g46,g209)
    c: Coincident(g98,g212)
    c: Coincident(g98,g224)
    c: Coincident(g57,g212)
    c: Coincident(g57,g244)
    c: Coincident(g66,g224)
    c: Coincident(g109,g244)
    c: Coincident(g66,g175)
    c: Coincident(g31,g109)
    c: Coincident(g173,g175)
    c: Coincident(g31,g210)
    c: Coincident(g43,g173)
    c: Coincident(g210,g232)
    c: Coincident(g43,g243)
    c: Coincident(g93,g232)
    c: Coincident(g93,g149)
    c: Coincident(g179,g243)
    c: Coincident(g129,g149)
    c: Coincident(g179,g230)
    c: Coincident(g129,g196)
    c: Coincident(g38,g46)
    c: Coincident(g182,g230)
    c: Coincident(g151,g196)
    c: Coincident(g38,g169)
    c: Coincident(g151,g217)
    c: Coincident(g131,g155)
    c: Coincident(g95,g182)
    c: Coincident(g15,g155)
    c: Coincident(g63,g169)
    c: Coincident(g217,g248)
    c: Coincident(g63,g130)
    c: Coincident(g15,g144)
    c: Coincident(g75,g130)
    c: Coincident(g52,g95)
    c: Coincident(g144,g223)
    c: Coincident(g19,g75)
    c: Coincident(g67,g248)
    c: Coincident(g19,g228)
    c: Coincident(g52,g184)
    c: Coincident(g207,g223)
    c: Coincident(g185,g228)
    c: Coincident(g44,g67)
    c: Coincident(g154,g207)
    c: Coincident(g185,g199)
    c: Coincident(g106,g184)
    c: Coincident(g199,g206)
    c: Coincident(g25,g44)
    c: Coincident(g83,g154)
    c: Coincident(g22,g106)
    c: Coincident(g167,g206)
    c: Coincident(g83,g134)
    c: Coincident(g25,g187)
    c: Coincident(g77,g167)
    c: Coincident(g22,g119)
    c: Coincident(g27,g134)
    c: Coincident(g77,g105)
    c: Coincident(g187,g215)
    c: Coincident(g11,g96)
    c: Coincident(g30,g180)
    c: Coincident(g30,g161)
    c: Coincident(g92,g161)
    c: Coincident(g116,g119)
    c: Coincident(g37,g92)
    c: Coincident(g37,g146)
    c: Coincident(g102,g105)
    c: Coincident(g146,g241)
    c: Coincident(g11,g49)
    c: Coincident(g215,g218)
    c: Coincident(g27,g252)
    c: Coincident(g5,g241)
    c: Coincident(g5,g32)
    c: Coincident(g49,g150)
    c: Coincident(g102,g116)
    c: Coincident(g32,g51)
    c: Coincident(g137,g218)
    c: Coincident(g51,g190)
    c: Coincident(g150,g234)
    c: Coincident(g221,g252)
    c: Coincident(g139,g190)
    c: Coincident(g115,g139)
    c: Coincident(g137,g197)
    c: Coincident(g141,g234)
    c: Coincident(g81,g221)
    c: Coincident(g81,g115)
    c: Coincident(g112,g141)
    c: Coincident(g178,g197)
    c: Coincident(g76,g112)
    c: Coincident(g86,g178)
    c: Coincident(g74,g76)
    c: Coincident(g86,g108)
    c: Coincident(g74,g198)
    c: Coincident(g6,g198)
    c: Coincident(g6,g91)
    c: Coincident(g108,g147)
    c: Coincident(g36,g91)
    c: Coincident(g36,g172)
    c: Coincident(g10,g172)
    c: Coincident(g10,g222)
    c: Coincident(g213,g222)
    c: Coincident(g147,g257)
    c: Coincident(g101,g213)
    c: Coincident(g101,g177)
    c: Coincident(g177,g229)
    c: Coincident(g163,g229)
    c: Coincident(g145,g163)
    c: Coincident(g145,g208)
    c: Coincident(g250,g257)
    c: Coincident(g211,g250)
    c: Coincident(g56,g208)
    c: Coincident(g7,g226)
    c: Coincident(g7,g56)
    c: Coincident(g168,g226)
    c: Coincident(g4,g211)
    c: Coincident(g143,g168)
    c: Coincident(g21,g143)
    c: Coincident(g21,g60)
    c: Coincident(g60,g104)
    c: Coincident(g61,g94)
    c: Coincident(g4,g94)
    c: Coincident(g71,g104)
    c: Coincident(g33,g71)
    c: Coincident(g33,g219)
    c: Coincident(g165,g219)
    c: Coincident(g162,g165)
    c: Coincident(g132,g162)
    c: Coincident(g3,g132)
    c: Coincident(g61,g200)
    c: Coincident(g3,g127)
    c: Coincident(g28,g127)
    c: Coincident(g28,g73)
    c: Coincident(g73,g148)
    c: Coincident(g107,g148)
    c: Coincident(g107,g176)
    c: Coincident(g121,g176)
    c: Coincident(g88,g121)
    c: Coincident(g88,g90)
    c: Coincident(g29,g200)
    c: Coincident(g68,g90)
    c: Coincident(g68,g233)
    c: Coincident(g122,g233)
    c: Coincident(g122,g133)
    c: Coincident(g64,g133)
    c: Coincident(g29,g110)
    c: Coincident(g26,g64)
    c: Coincident(g26,g35)
    c: Coincident(g54,g110)
    c: Coincident(g35,g171)
    c: Coincident(g171,g195)
    c: Coincident(g54,g216)
    c: Coincident(g40,g195)
    c: Coincident(g16,g40)
    c: Coincident(g16,g225)
    c: Coincident(g85,g216)
    c: Coincident(g181,g225)
    c: Coincident(g20,g70)
    c: Coincident(g20,g153)
    c: Coincident(g70,g239)
    c: Coincident(g17,g153)
    c: Coincident(g18,g181)
    c: Coincident(g41,g85)
    c: Coincident(g2,g239)
    c: Coincident(g17,g135)
    c: Coincident(g18,g87)
    c: Coincident(g2,g204)
    c: Coincident(g87,g160)
    c: Coincident(g111,g135)
    c: Coincident(g158,g204)
    c: Coincident(g34,g41)
    c: Coincident(g84,g160)
    c: Coincident(g158,g245)
    c: Coincident(g111,g117)
    c: Coincident(g231,g254)
    c: Coincident(g84,g123)
    c: Coincident(g125,g245)
    c: Coincident(g50,g125)
    c: Coincident(g14,g123)
    c: Coincident(g117,g227)
    c: Coincident(g34,g62)
    c: Coincident(g14,g142)
    c: Coincident(g50,g97)
    c: Coincident(g0,g231)
    c: Coincident(g55,g97)
    c: Coincident(g120,g142)
    c: Coincident(g55,g59)
    c: Coincident(g59,g128)
    c: Coincident(g80,g254)
    c: Coincident(g128,g253)
    c: Coincident(g152,g253)
    c: Coincident(g152,g193)
    c: Coincident(g193,g194)
    c: Coincident(g45,g227)
    c: Coincident(g24,g120)
    c: Coincident(g53,g62)
    c: Coincident(g0,g136)
    c: Coincident(g45,g58)
    c: Coincident(g80,g201)
    c: Coincident(g136,g188)
    c: Coincident(g53,g235)
    c: Coincident(g47,g58)
    c: Coincident(g188,g256)
    c: Coincident(g82,g201)
    c: Coincident(g47,g69)
    c: Coincident(g8,g235)
    c: Coincident(g166,g256)
    c: Coincident(g82,g205)
    c: Coincident(g166,g186)
    c: Coincident(g13,g69)
    c: Coincident(g8,g39)
    c: Coincident(g13,g72)
    c: Coincident(g170,g186)
    c: Coincident(g72,g78)
    c: Coincident(g183,g205)
    c: Coincident(g157,g170)
    c: Coincident(g78,g246)
    c: Coincident(g39,g65)
    c: Coincident(g99,g246)
    c: Coincident(g157,g251)
    c: Coincident(g99,g124)
    c: Coincident(g126,g183)
    c: Coincident(g236,g251)
    c: Coincident(g124,g156)
    c: Coincident(g89,g236)
    c: Coincident(g156,g247)
    c: Coincident(g65,g118)
    c: Coincident(g191,g247)
    c: Coincident(g89,g240)
    c: Coincident(g113,g126)
    c: Coincident(g114,g191)
    c: Coincident(g1,g114)
    c: Coincident(g202,g240)
    c: Coincident(g48,g202)
    c: Coincident(g9,g113)
    c: Coincident(g118,g220)
    c: Coincident(g9,g249)
    c: Coincident(g220,g255)
    c: Coincident(g192,g249)
    c: Coincident(g214,g255)
    c: Coincident(g138,g192)
    c: Coincident(g42,g214)
    c: Coincident(g42,g238)
    c: Coincident(g138,g189)
    c: Coincident(g140,g238)
    c: Coincident(g174,g189)
    c: Coincident(g100,g140)
    c: Coincident(g159,g174)
    c: Coincident(g100,g242)
    c: Coincident(g12,g159)
    c: Coincident(g79,g242)
    c: Coincident(g12,g23)
    c: Coincident(g24,g103)
    c: Coincident(g103,g194)
    c: Coincident(g1,g203)
    c: Coincident(g48,g203)
    c: Coincident(g79,g164)
    c: Coincident(g23,g164)
FEATURE [App::Part] Board_Geoms_931
  Group = -> [Pcb_931,PCB_Sketch_931]
  Origin = -> Origin
FEATURE [Part::Feature] Shape  label="R21_C_0402_1005Metric_38c94f1f1ba7"
  Placement = pos=(189.8,-128.5,0) rot=(0,0,1;3.14159rad)
  shape: bbox 1 x 0.5 x 0.5 mm, 28 faces (baked)
FEATURE [App::Link] R21_C_0402_1005Metric_38c94f1f1ba7_ln_  label="R20_C_0402_1005Metric_7b8d80ad2dcc"
  LinkPlacement = pos=(189.9,-114.1,0) rot=(0,0,1;3.14159rad)
  LinkedObject = -> Shape
  Placement = pos=(189.9,-114.1,0) rot=(0,0,1;3.14159rad)
FEATURE [App::Link] R21_C_0402_1005Metric_38c94f1f1ba7_ln_001  label="C1_C_0402_1005Metric_d29c508b4b60"
  LinkPlacement = pos=(195.2,-70.7,0) rot=(0,0,1;0rad)
  LinkedObject = -> Shape
  Placement = pos=(195.2,-70.7,0) rot=(0,0,1;0rad)
FEATURE [Part::Feature] Shape001  label="R19_R_0402_1005Metric_9ca80ee487fc"
  Placement = pos=(194.8,-102.6,0) rot=(0,0,-1;1.5708rad)
  shape: bbox 0.5 x 1 x 0.35 mm, 26 faces (baked)
FEATURE [App::Link] R21_C_0402_1005Metric_38c94f1f1ba7_ln_002  label="C9_C_0402_1005Metric_a875c5e367f2"
  LinkPlacement = pos=(190.3,-80.1,0) rot=(0,0,-1;1.5708rad)
  LinkedObject = -> Shape
  Placement = pos=(190.3,-80.1,0) rot=(0,0,-1;1.5708rad)
FEATURE [Part::Feature] Shape002  label="D2_D_SMA_34cf3897dfc1"
  Placement = pos=(195.2,-118,0) rot=(0,0,-1;1.5708rad)
  shape: bbox 2.7 x 5 x 2.22 mm, 41 faces (baked)
FEATURE [Part::Feature] Shape003  label="C42_C_0603_1608Metric_3f0e18eb3bdb"
  Placement = pos=(197,-72.4,0) rot=(0,0,1;1.5708rad)
  shape: bbox 0.8 x 1.6 x 0.8 mm, 28 faces (baked)
FEATURE [Part::Feature] Shape004  label="SW3_Fillet_54ad2342c7e7"
  Placement = pos=(195.3,-140.21,0) rot=(0,0,1;3.14159rad)
  shape: bbox 8.3 x 20.48 x 8.6 mm, 32 faces (baked)
FEATURE [Part::Feature] Shape005  label="U5_SOT_223_0bc22c24d438"
  Placement = pos=(202.5,-74.4,0) rot=(0,0,1;0rad)
  shape: bbox 7 x 6.5 x 1.7 mm, 78 faces (baked)
FEATURE [App::Link] R19_R_0402_1005Metric_9ca80ee487fc_ln_  label="R2_R_0402_1005Metric_dea8e135976e"
  LinkPlacement = pos=(201.5,-68.7,0) rot=(0,0,1;1.5708rad)
  LinkedObject = -> Shape001
  Placement = pos=(201.5,-68.7,0) rot=(0,0,1;1.5708rad)
FEATURE [App::Link] C42_C_0603_1608Metric_3f0e18eb3bdb_ln_  label="C45_C_0603_1608Metric_d322fa890f2c"
  LinkPlacement = pos=(188.9,-123.4,0) rot=(0,0,1;0rad)
  LinkedObject = -> Shape003
  Placement = pos=(188.9,-123.4,0) rot=(0,0,1;0rad)
FEATURE [App::Link] R21_C_0402_1005Metric_38c94f1f1ba7_ln_003  label="C46_C_0402_1005Metric_a9bfb0d6892e"
  LinkPlacement = pos=(189.1,-100.1,0) rot=(0,0,1;0rad)
  LinkedObject = -> Shape
  Placement = pos=(189.1,-100.1,0) rot=(0,0,1;0rad)
FEATURE [App::Link] R19_R_0402_1005Metric_9ca80ee487fc_ln_001  label="R15_R_0402_1005Metric_e6cf502f8789"
  LinkPlacement = pos=(187.7,-106.9,0) rot=(0,0,-1;1.5708rad)
  LinkedObject = -> Shape001
  Placement = pos=(187.7,-106.9,0) rot=(0,0,-1;1.5708rad)
FEATURE [Part::Feature] Shape006  label="C44_C_1206_3216Metric_504a53cc2dd0"
  Placement = pos=(190.5,-133.025,0) rot=(0,0,-1;1.5708rad)
  shape: bbox 1.6 x 3.2 x 1.6 mm, 28 faces (baked)
FEATURE [App::Link] R21_C_0402_1005Metric_38c94f1f1ba7_ln_004  label="C18_C_0402_1005Metric_92a1be41be9e"
  LinkPlacement = pos=(189.4,-106.5,0) rot=(0,0,1;0rad)
  LinkedObject = -> Shape
  Placement = pos=(189.4,-106.5,0) rot=(0,0,1;0rad)
FEATURE [App::Link] R21_C_0402_1005Metric_38c94f1f1ba7_ln_005  label="C31_C_0402_1005Metric_578c4d3870ae"
  LinkPlacement = pos=(189,-90,0) rot=(0,0,1;3.14159rad)
  LinkedObject = -> Shape
  Placement = pos=(189,-90,0) rot=(0,0,1;3.14159rad)
FEATURE [App::Link] R19_R_0402_1005Metric_9ca80ee487fc_ln_002  label="R3_R_0402_1005Metric_969b0b0747f2"
  LinkPlacement = pos=(191.3,-80.09,0) rot=(0,0,-1;1.5708rad)
  LinkedObject = -> Shape001
  Placement = pos=(191.3,-80.09,0) rot=(0,0,-1;1.5708rad)
FEATURE [App::Link] R21_C_0402_1005Metric_38c94f1f1ba7_ln_006  label="C29_C_0402_1005Metric_878fa2face33"
  LinkPlacement = pos=(185.6,-86.9,0) rot=(0,0,1;1.5708rad)
  LinkedObject = -> Shape
  Placement = pos=(185.6,-86.9,0) rot=(0,0,1;1.5708rad)
FEATURE [Part::Feature] Shape007  label="U6_QFN-20-1EP_4x4mm_Pitch0.5mm_3f7a39cb167c"
  Placement = pos=(190.975,-103.35,0) rot=(0,0,1;1.5708rad)
  shape: bbox 4 x 4 x 0.77 mm, 134 faces (baked)
FEATURE [App::Link] R19_R_0402_1005Metric_9ca80ee487fc_ln_003  label="R18_R_0402_1005Metric_e9874ca0240e"
  LinkPlacement = pos=(195.4,-53,0) rot=(0,0,1;1.5708rad)
  LinkedObject = -> Shape001
  Placement = pos=(195.4,-53,0) rot=(0,0,1;1.5708rad)
FEATURE [App::Link] R19_R_0402_1005Metric_9ca80ee487fc_ln_004  label="R7_R_0402_1005Metric_0d6ee2aba382"
  LinkPlacement = pos=(196.1,-57,0) rot=(0,0,-1;1.5708rad)
  LinkedObject = -> Shape001
  Placement = pos=(196.1,-57,0) rot=(0,0,-1;1.5708rad)
FEATURE [Part::Feature] Shape008  label="L3_L_0402_1005Metric_7322f57e24a3"
  Placement = pos=(191.1,-99,0) rot=(0,0,1;3.14159rad)
  shape: bbox 1 x 0.5 x 0.5 mm, 28 faces (baked)
FEATURE [App::Link] C42_C_0603_1608Metric_3f0e18eb3bdb_ln_001  label="C26_C_0603_1608Metric_e24a75b1fd6c"
  LinkPlacement = pos=(196.7,-53.6,0) rot=(0,0,-1;1.5708rad)
  LinkedObject = -> Shape003
  Placement = pos=(196.7,-53.6,0) rot=(0,0,-1;1.5708rad)
FEATURE [App::Link] R21_C_0402_1005Metric_38c94f1f1ba7_ln_007  label="C41_C_0402_1005Metric_e05767d0328b"
  LinkPlacement = pos=(196.7,-101.5,0) rot=(0,0,1;1.5708rad)
  LinkedObject = -> Shape
  Placement = pos=(196.7,-101.5,0) rot=(0,0,1;1.5708rad)
FEATURE [App::Link] R19_R_0402_1005Metric_9ca80ee487fc_ln_005  label="R6_R_0402_1005Metric_11a2181a152e"
  LinkPlacement = pos=(195.1,-57,0) rot=(0,0,-1;1.5708rad)
  LinkedObject = -> Shape001
  Placement = pos=(195.1,-57,0) rot=(0,0,-1;1.5708rad)
FEATURE [App::Link] C44_C_1206_3216Metric_504a53cc2dd0_ln_  label="C15_C_1206_3216Metric_4eda32e8580f"
  LinkPlacement = pos=(204.5,-79.3,0) rot=(0,0,1;0rad)
  LinkedObject = -> Shape006
  Placement = pos=(204.5,-79.3,0) rot=(0,0,1;0rad)
FEATURE [App::Link] C44_C_1206_3216Metric_504a53cc2dd0_ln_001  label="C22_C_1206_3216Metric_2920babed859"
  LinkPlacement = pos=(204.4,-81.8,0) rot=(0,0,1;0rad)
  LinkedObject = -> Shape006
  Placement = pos=(204.4,-81.8,0) rot=(0,0,1;0rad)
FEATURE [App::Link] R19_R_0402_1005Metric_9ca80ee487fc_ln_006  label="R23_R_0402_1005Metric_7dfb490c449e"
  LinkPlacement = pos=(184.1,-52.41,0) rot=(0,0,1;1.5708rad)
  LinkedObject = -> Shape001
  Placement = pos=(184.1,-52.41,0) rot=(0,0,1;1.5708rad)
FEATURE [Part::Feature] Shape009  label="D516_LED_0603_1608Metric_23db4c450fc7"
  Placement = pos=(189.1,-126.2,0) rot=(0,0,1;1.5708rad)
  shape: bbox 0.8 x 1.6 x 1.1 mm, 50 faces (baked)
FEATURE [App::Link] R21_C_0402_1005Metric_38c94f1f1ba7_ln_008  label="C16_C_0402_1005Metric_ccc6f5fbae95"
  LinkPlacement = pos=(192.7,-132.7,0) rot=(0,0,1;1.5708rad)
  LinkedObject = -> Shape
  Placement = pos=(192.7,-132.7,0) rot=(0,0,1;1.5708rad)
FEATURE [App::Link] R21_C_0402_1005Metric_38c94f1f1ba7_ln_009  label="C20_C_0402_1005Metric_339430b002f9"
  LinkPlacement = pos=(204.7,-53.1,0) rot=(0,0,1;3.14159rad)
  LinkedObject = -> Shape
  Placement = pos=(204.7,-53.1,0) rot=(0,0,1;3.14159rad)
FEATURE [App::Link] R21_C_0402_1005Metric_38c94f1f1ba7_ln_010  label="C47_C_0402_1005Metric_af42fe187c16"
  LinkPlacement = pos=(195,-99.9,0) rot=(0,0,1;0rad)
  LinkedObject = -> Shape
  Placement = pos=(195,-99.9,0) rot=(0,0,1;0rad)
FEATURE [Part::Feature] Shape010  label="U8_SOT_23_1e3b1a0e5d43"
  Placement = pos=(193.9,-128,0) rot=(0,0,1;3.14159rad)
  shape: bbox 2.5 x 3 x 1.2 mm, 76 faces (baked)
FEATURE [App::Link] R21_C_0402_1005Metric_38c94f1f1ba7_ln_011  label="C6_C_0402_1005Metric_7f7ff18c55e3"
  LinkPlacement = pos=(190.5,-68.8,0) rot=(0,0,1;3.14159rad)
  LinkedObject = -> Shape
  Placement = pos=(190.5,-68.8,0) rot=(0,0,1;3.14159rad)
FEATURE [App::Link] D2_D_SMA_34cf3897dfc1_ln_  label="D1_D_SMA_3cb871b8a290"
  LinkPlacement = pos=(190.3,-109.8,0) rot=(0,0,1;3.14159rad)
  LinkedObject = -> Shape002
  Placement = pos=(190.3,-109.8,0) rot=(0,0,1;3.14159rad)
FEATURE [Part::Feature] Shape011  label="U3_QFN_56_1EP_7x7mm_P04mm_EP32x32mm_92a982e71d8d"
  Placement = pos=(189.6,-74.9,0) rot=(0,0,1;0rad)
  shape: bbox 7 x 7 x 0.95 mm, 350 faces (baked)
FEATURE [App::Link] R21_C_0402_1005Metric_38c94f1f1ba7_ln_012  label="C30_C_0402_1005Metric_cc59a400e17a"
  LinkPlacement = pos=(191,-90,0) rot=(0,0,1;3.14159rad)
  LinkedObject = -> Shape
  Placement = pos=(191,-90,0) rot=(0,0,1;3.14159rad)
FEATURE [App::Link] R21_C_0402_1005Metric_38c94f1f1ba7_ln_013  label="C13_C_0402_1005Metric_d2173120320b"
  LinkPlacement = pos=(198.8,-57.6,0) rot=(0,0,1;3.14159rad)
  LinkedObject = -> Shape
  Placement = pos=(198.8,-57.6,0) rot=(0,0,1;3.14159rad)
FEATURE [App::Link] L3_L_0402_1005Metric_7322f57e24a3_ln_  label="L4_L_0402_1005Metric_e4c50960bfc8"
  LinkPlacement = pos=(190.7,-97.6,0) rot=(0,0,1;0rad)
  LinkedObject = -> Shape008
  Placement = pos=(190.7,-97.6,0) rot=(0,0,1;0rad)
FEATURE [App::Link] R21_C_0402_1005Metric_38c94f1f1ba7_ln_014  label="C2_C_0402_1005Metric_4b4f118f5010"
  LinkPlacement = pos=(185.6,-81.3,0) rot=(0,0,1;3.14159rad)
  LinkedObject = -> Shape
  Placement = pos=(185.6,-81.3,0) rot=(0,0,1;3.14159rad)
FEATURE [App::Link] D516_LED_0603_1608Metric_23db4c450fc7_ln_  label="D517_LED_0603_1608Metric_b24ae36cc63a"
  LinkPlacement = pos=(190.7,-126.2,0) rot=(0,0,1;1.5708rad)
  LinkedObject = -> Shape009
  Placement = pos=(190.7,-126.2,0) rot=(0,0,1;1.5708rad)
FEATURE [App::Link] R21_C_0402_1005Metric_38c94f1f1ba7_ln_015  label="C10_C_0402_1005Metric_25fd1e42a1bf"
  LinkPlacement = pos=(186.1,-69.6,0) rot=(0,0,1;1.5708rad)
  LinkedObject = -> Shape
  Placement = pos=(186.1,-69.6,0) rot=(0,0,1;1.5708rad)
FEATURE [App::Link] R21_C_0402_1005Metric_38c94f1f1ba7_ln_016  label="C33_C_0402_1005Metric_872bb8822931"
  LinkPlacement = pos=(204.2,-51.5,0) rot=(0,0,-1;1.5708rad)
  LinkedObject = -> Shape
  Placement = pos=(204.2,-51.5,0) rot=(0,0,-1;1.5708rad)
FEATURE [App::Link] R21_C_0402_1005Metric_38c94f1f1ba7_ln_017  label="C43_C_0402_1005Metric_b465c88a99c7"
  LinkPlacement = pos=(202.2,-129.1,0) rot=(0,0,-1;1.5708rad)
  LinkedObject = -> Shape
  Placement = pos=(202.2,-129.1,0) rot=(0,0,-1;1.5708rad)
FEATURE [App::Link] R19_R_0402_1005Metric_9ca80ee487fc_ln_007  label="R4_R_0402_1005Metric_18a2017ffd4b"
  LinkPlacement = pos=(194,-57,0) rot=(0,0,-1;1.5708rad)
  LinkedObject = -> Shape001
  Placement = pos=(194,-57,0) rot=(0,0,-1;1.5708rad)
FEATURE [App::Link] C44_C_1206_3216Metric_504a53cc2dd0_ln_002  label="C25_C_1206_3216Metric_a9b05d8d3b1b"
  LinkPlacement = pos=(199.6,-132.5,0) rot=(0,0,1;0rad)
  LinkedObject = -> Shape006
  Placement = pos=(199.6,-132.5,0) rot=(0,0,1;0rad)
FEATURE [Part::Feature] Shape012  label="Y1_Crystal_SMD_3225-4Pin_3.2x2.5mm_5bc66405eca2"
  Placement = pos=(186.9,-83.7,0) rot=(0,0,1;0rad)
  shape: bbox 3.2 x 2.501 x 0.64 mm, 28 faces (baked)
FEATURE [App::Link] R19_R_0402_1005Metric_9ca80ee487fc_ln_008  label="R16_R_0402_1005Metric_1ac23e3eb529"
  LinkPlacement = pos=(205.3,-51.5,0) rot=(0,0,-1;1.5708rad)
  LinkedObject = -> Shape001
  Placement = pos=(205.3,-51.5,0) rot=(0,0,-1;1.5708rad)
FEATURE [App::Link] R19_R_0402_1005Metric_9ca80ee487fc_ln_009  label="Q1_R_0402_1005Metric_19db146f615e"
  LinkPlacement = pos=(204.7,-50,0) rot=(0,0,1;0rad)
  LinkedObject = -> Shape001
  Placement = pos=(204.7,-50,0) rot=(0,0,1;0rad)
FEATURE [App::Link] U8_SOT_23_1e3b1a0e5d43_ln_  label="Q2_SOT_23_816b0a6423d4"
  LinkPlacement = pos=(191.1,-56.8,0) rot=(0,0,1;1.5708rad)
  LinkedObject = -> Shape010
  Placement = pos=(191.1,-56.8,0) rot=(0,0,1;1.5708rad)
FEATURE [App::Link] R21_C_0402_1005Metric_38c94f1f1ba7_ln_018  label="C24_C_0402_1005Metric_c74ed45d8278"
  LinkPlacement = pos=(196.3,-103.1,0) rot=(0,0,1;0rad)
  LinkedObject = -> Shape
  Placement = pos=(196.3,-103.1,0) rot=(0,0,1;0rad)
FEATURE [App::Link] C44_C_1206_3216Metric_504a53cc2dd0_ln_003  label="C35_C_1206_3216Metric_0a151451740c"
  LinkPlacement = pos=(201.1,-105.5,0) rot=(0,0,1;1.5708rad)
  LinkedObject = -> Shape006
  Placement = pos=(201.1,-105.5,0) rot=(0,0,1;1.5708rad)
FEATURE [App::Link] R21_C_0402_1005Metric_38c94f1f1ba7_ln_019  label="R22_C_0402_1005Metric_0e379b04b221"
  LinkPlacement = pos=(195.3,-65,0) rot=(0,0,1;0rad)
  LinkedObject = -> Shape
  Placement = pos=(195.3,-65,0) rot=(0,0,1;0rad)
FEATURE [App::Link] R19_R_0402_1005Metric_9ca80ee487fc_ln_010  label="R17_R_0402_1005Metric_c84f106557fc"
  LinkPlacement = pos=(193.4,-52.99,0) rot=(0,0,1;1.5708rad)
  LinkedObject = -> Shape001
  Placement = pos=(193.4,-52.99,0) rot=(0,0,1;1.5708rad)
FEATURE [App::Link] R21_C_0402_1005Metric_38c94f1f1ba7_ln_020  label="C34_C_0402_1005Metric_69e14d7ecb16"
  LinkPlacement = pos=(200.7,-51.3,0) rot=(0,0,-1;1.5708rad)
  LinkedObject = -> Shape
  Placement = pos=(200.7,-51.3,0) rot=(0,0,-1;1.5708rad)
FEATURE [App::Link] R21_C_0402_1005Metric_38c94f1f1ba7_ln_021  label="C32_C_0402_1005Metric_dab31895c2db"
  LinkPlacement = pos=(187,-90,0) rot=(0,0,1;3.14159rad)
  LinkedObject = -> Shape
  Placement = pos=(187,-90,0) rot=(0,0,1;3.14159rad)
FEATURE [App::Link] R21_C_0402_1005Metric_38c94f1f1ba7_ln_022  label="C23_C_0402_1005Metric_a91c703b8113"
  LinkPlacement = pos=(195,-100.9,0) rot=(0,0,1;3.14159rad)
  LinkedObject = -> Shape
  Placement = pos=(195,-100.9,0) rot=(0,0,1;3.14159rad)
FEATURE [Part::Feature] Shape013  label="J4_PinHeader_2x07_P127mm_Vertical_bf31e59c633b"
  Placement = pos=(194.765,-81.49,0) rot=(0,0,1;0rad)
  shape: bbox 3.4 x 8.89 x 6.3 mm, 298 faces (baked)
FEATURE [App::Link] R21_C_0402_1005Metric_38c94f1f1ba7_ln_023  label="C11_C_0402_1005Metric_ee0f1353bdd2"
  LinkPlacement = pos=(192.4,-68.8,0) rot=(0,0,1;0rad)
  LinkedObject = -> Shape
  Placement = pos=(192.4,-68.8,0) rot=(0,0,1;0rad)
FEATURE [App::Link] R19_R_0402_1005Metric_9ca80ee487fc_ln_011  label="R12_R_0402_1005Metric_1dd42002f4d0"
  LinkPlacement = pos=(200.1,-129.09,0) rot=(0,0,1;1.5708rad)
  LinkedObject = -> Shape001
  Placement = pos=(200.1,-129.09,0) rot=(0,0,1;1.5708rad)
FEATURE [App::Link] R21_C_0402_1005Metric_38c94f1f1ba7_ln_024  label="C27_C_0402_1005Metric_39aa6632ecb3"
  LinkPlacement = pos=(192.72,-97.6,0) rot=(0,0,1;0rad)
  LinkedObject = -> Shape
  Placement = pos=(192.72,-97.6,0) rot=(0,0,1;0rad)
FEATURE [App::Link] R19_R_0402_1005Metric_9ca80ee487fc_ln_012  label="R5_R_0402_1005Metric_a55a78cb6167"
  LinkPlacement = pos=(197.2,-57,0) rot=(0,0,-1;1.5708rad)
  LinkedObject = -> Shape001
  Placement = pos=(197.2,-57,0) rot=(0,0,-1;1.5708rad)
FEATURE [App::Link] R19_R_0402_1005Metric_9ca80ee487fc_ln_013  label="R1_R_0402_1005Metric_f5b816f9472f"
  LinkPlacement = pos=(199.8,-69.2,0) rot=(0,0,1;0rad)
  LinkedObject = -> Shape001
  Placement = pos=(199.8,-69.2,0) rot=(0,0,1;0rad)
FEATURE [App::Link] D516_LED_0603_1608Metric_23db4c450fc7_ln_001  label="D518_LED_0603_1608Metric_9ded9605b13f"
  LinkPlacement = pos=(195.4,-63.5,0) rot=(0,0,1;0rad)
  LinkedObject = -> Shape009
  Placement = pos=(195.4,-63.5,0) rot=(0,0,1;0rad)
FEATURE [App::Link] C44_C_1206_3216Metric_504a53cc2dd0_ln_004  label="C21_C_1206_3216Metric_429a80aec131"
  LinkPlacement = pos=(194.9,-112.9,0) rot=(0,0,1;3.14159rad)
  LinkedObject = -> Shape006
  Placement = pos=(194.9,-112.9,0) rot=(0,0,1;3.14159rad)
FEATURE [Part::Feature] Shape014  label="U9_SOT_23_6_c7a49d86fbfe"
  Placement = pos=(188.6,-87.6,0) rot=(0,0,1;3.14159rad)
  shape: bbox 2.8 x 2.9 x 1.55 mm, 124 faces (baked)
FEATURE [App::Link] R21_C_0402_1005Metric_38c94f1f1ba7_ln_025  label="C17_C_0402_1005Metric_54b876e493f1"
  LinkPlacement = pos=(189.4,-107.5,0) rot=(0,0,1;0rad)
  LinkedObject = -> Shape
  Placement = pos=(189.4,-107.5,0) rot=(0,0,1;0rad)
FEATURE [Part::Feature] Shape015  label="SW1_SW_SPST_PTS645_03fdbfd9ae36"
  Placement = pos=(200.6,-63,0) rot=(0,0,-1;1.5708rad)
  shape: bbox 6 x 9 x 4.3 mm, 97 faces (baked)
FEATURE [App::Link] R19_R_0402_1005Metric_9ca80ee487fc_ln_014  label="R24_R_0402_1005Metric_04ceae6545c3"
  LinkPlacement = pos=(188.2,-57.7,0) rot=(0,0,-1;1.5708rad)
  LinkedObject = -> Shape001
  Placement = pos=(188.2,-57.7,0) rot=(0,0,-1;1.5708rad)
FEATURE [App::Link] Y1_Crystal_SMD_3225_4Pin_3_2x2_5mm_5bc66405eca2_ln_  label="Y2_Crystal_SMD_3225-4Pin_3.2x2.5mm_c0e7deee875b"
  LinkPlacement = pos=(195.8,-105.9,0) rot=(0,0,1;1.5708rad)
  LinkedObject = -> Shape012
  Placement = pos=(195.8,-105.9,0) rot=(0,0,1;1.5708rad)
FEATURE [App::Link] R19_R_0402_1005Metric_9ca80ee487fc_ln_015  label="R10_R_0402_1005Metric_299a858bebda"
  LinkPlacement = pos=(195.5,-77.1,0) rot=(0,0,1;1.5708rad)
  LinkedObject = -> Shape001
  Placement = pos=(195.5,-77.1,0) rot=(0,0,1;1.5708rad)
FEATURE [App::Link] R19_R_0402_1005Metric_9ca80ee487fc_ln_016  label="R9_R_0402_1005Metric_84cfa7eb0e8e"
  LinkPlacement = pos=(198.9,-129.1,0) rot=(0,0,-1;1.5708rad)
  LinkedObject = -> Shape001
  Placement = pos=(198.9,-129.1,0) rot=(0,0,-1;1.5708rad)
FEATURE [App::Link] R21_C_0402_1005Metric_38c94f1f1ba7_ln_026  label="C28_C_0402_1005Metric_fdbb3c7674a5"
  LinkPlacement = pos=(194.2,-98.1,0) rot=(0,0,1;1.5708rad)
  LinkedObject = -> Shape
  Placement = pos=(194.2,-98.1,0) rot=(0,0,1;1.5708rad)
FEATURE [App::Link] R19_R_0402_1005Metric_9ca80ee487fc_ln_017  label="R11_R_0402_1005Metric_60fb483f3fd5"
  LinkPlacement = pos=(196.7,-77.1,0) rot=(0,0,-1;1.5708rad)
  LinkedObject = -> Shape001
  Placement = pos=(196.7,-77.1,0) rot=(0,0,-1;1.5708rad)
FEATURE [App::Link] R21_C_0402_1005Metric_38c94f1f1ba7_ln_027  label="C4_C_0402_1005Metric_564747b89293"
  LinkPlacement = pos=(187.92,-81.4,0) rot=(0,0,1;0rad)
  LinkedObject = -> Shape
  Placement = pos=(187.92,-81.4,0) rot=(0,0,1;0rad)
FEATURE [Part::Feature] Shape016  label="L1_Sf㱟fd_sp_e828286b0ac3"
  Placement = pos=(200.4,-114.7,0) rot=(0,0,1;1.5708rad)
  shape: bbox 7.058 x 7.058 x 2.5 mm, 79 faces (baked)
FEATURE [App::Link] L3_L_0402_1005Metric_7322f57e24a3_ln_001  label="L2_L_0402_1005Metric_cbc56b11f79b"
  LinkPlacement = pos=(192,-100.1,0) rot=(0,0,1;3.14159rad)
  LinkedObject = -> Shape008
  Placement = pos=(192,-100.1,0) rot=(0,0,1;3.14159rad)
FEATURE [App::Link] R19_R_0402_1005Metric_9ca80ee487fc_ln_018  label="R8_R_0402_1005Metric_044c423f79ff"
  LinkPlacement = pos=(197.8,-129.1,0) rot=(0,0,1;1.5708rad)
  LinkedObject = -> Shape001
  Placement = pos=(197.8,-129.1,0) rot=(0,0,1;1.5708rad)
FEATURE [App::Link] R21_C_0402_1005Metric_38c94f1f1ba7_ln_028  label="C5_C_0402_1005Metric_ff954b7ecdeb"
  LinkPlacement = pos=(190.5,-69.9,0) rot=(0,0,1;3.14159rad)
  LinkedObject = -> Shape
  Placement = pos=(190.5,-69.9,0) rot=(0,0,1;3.14159rad)
FEATURE [App::Link] R19_R_0402_1005Metric_9ca80ee487fc_ln_019  label="R14_R_0402_1005Metric_07a2d9395c6f"
  LinkPlacement = pos=(206.4,-51.5,0) rot=(0,0,-1;1.5708rad)
  LinkedObject = -> Shape001
  Placement = pos=(206.4,-51.5,0) rot=(0,0,-1;1.5708rad)
FEATURE [App::Link] R19_R_0402_1005Metric_9ca80ee487fc_ln_020  label="R13_R_0402_1005Metric_6ddea6fc7991"
  LinkPlacement = pos=(201.1,-129.1,0) rot=(0,0,-1;1.5708rad)
  LinkedObject = -> Shape001
  Placement = pos=(201.1,-129.1,0) rot=(0,0,-1;1.5708rad)
FEATURE [App::Part] Top_931
  Group = -> [Shape,R21_C_0402_1005Metric_38c94f1f1ba7_ln_,R21_C_0402_1005Metric_38c94f1f1ba7_ln_001,Shape001,R21_C_0402_1005Metric_38c94f1f1ba7_ln_002,Shape002,Shape003,Shape004,Shape005,R19_R_0402_1005Metric_9ca80ee487fc_ln_,C42_C_0603_1608Metric_3f0e18eb3bdb_ln_,R21_C_0402_1005Metric_38c94f1f1ba7_ln_003,R19_R_0402_1005Metric_9ca80ee487fc_ln_001,Shape006,R21_C_0402_1005Metric_38c94f1f1ba7_ln_004,+66 more]
  Origin = -> Origin003
FEATURE [Part::Feature] Shape017  label="BT1_MPD_BH_18650_PC2_17c3f7ae5d37"
  Placement = pos=(195.3,-132,-1.6) rot=(0.707107,0.707107,0;3.14159rad)
  shape: bbox 20.9 x 77.7 x 22.2 mm, 62 faces (baked)
FEATURE [Part::Feature] Shape018  label="J1_USB_Mini-B_Lumberg_2486_01_Horizontal_f06c414dff7d"
  Placement = pos=(195.3,-50.6,-1.6) rot=(1,0,0;3.14159rad)
  shape: bbox 9.9 x 9.2 x 4.997 mm, 472 faces (baked)
FEATURE [App::Part] Bot_931
  Group = -> [Shape017,Shape018]
  Origin = -> Origin004
FEATURE [App::Part] Step_Models_931
  Group = -> [Top_931,Bot_931]
  Origin = -> Origin002
FEATURE [App::Part] Board_931  label="ButterflyBadge"
  Group = -> [Local_CS_931,Board_Geoms_931,Step_Models_931]
  Origin = -> Origin001
